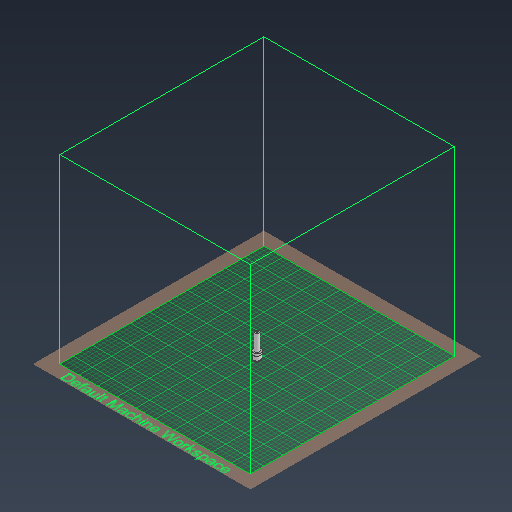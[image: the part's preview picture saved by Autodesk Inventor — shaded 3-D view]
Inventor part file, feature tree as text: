
AUTODESK INVENTOR PART (.ipt)
format: ipt  version: 2021 (Build 250183000, 183)  size: 282,624 bytes
history: native  units: mm
features: extrude x6, sketch x6
ambient origin geometry x8: Origin, YZ Plane, XZ Plane, XY Plane, X Axis, Y Axis, Z Axis, Center Point
bodies: Volumenkörper1 (feature_tree)
feature tree (12):
  extrude  "Extrusion1"  Depth=9.5mm
  extrude  "Extrusion2"  Depth=3.0mm
  extrude  "Extrusion5"  Depth=10.0mm
  extrude  "Extrusion6"  Depth=5.0mm
  extrude  "Extrusion7"  Depth=5.0mm
  extrude  "Extrusion8"  Depth=5.0mm
  sketch  "Skizze1"  dims[d0=9.5mm d1=9.5mm]
  sketch  "Skizze2"  dims[d2=3.0mm d3=0.0mm d4=14.8mm]
  sketch  "Skizze5"  dims[d5=10.0mm d6=0.0mm d13=4.0mm]
  sketch  "Skizze6"  dims[d14=5.0mm d15=0.0mm d16=17.0mm]
  sketch  "Skizze7"  dims[d17=5.0mm d18=0.0mm d19=9.8mm]
  sketch  "Skizze8"  dims[d20=36.0mm d21=0.0mm d22=4.0mm d23=5.0mm d24=0.0mm]
